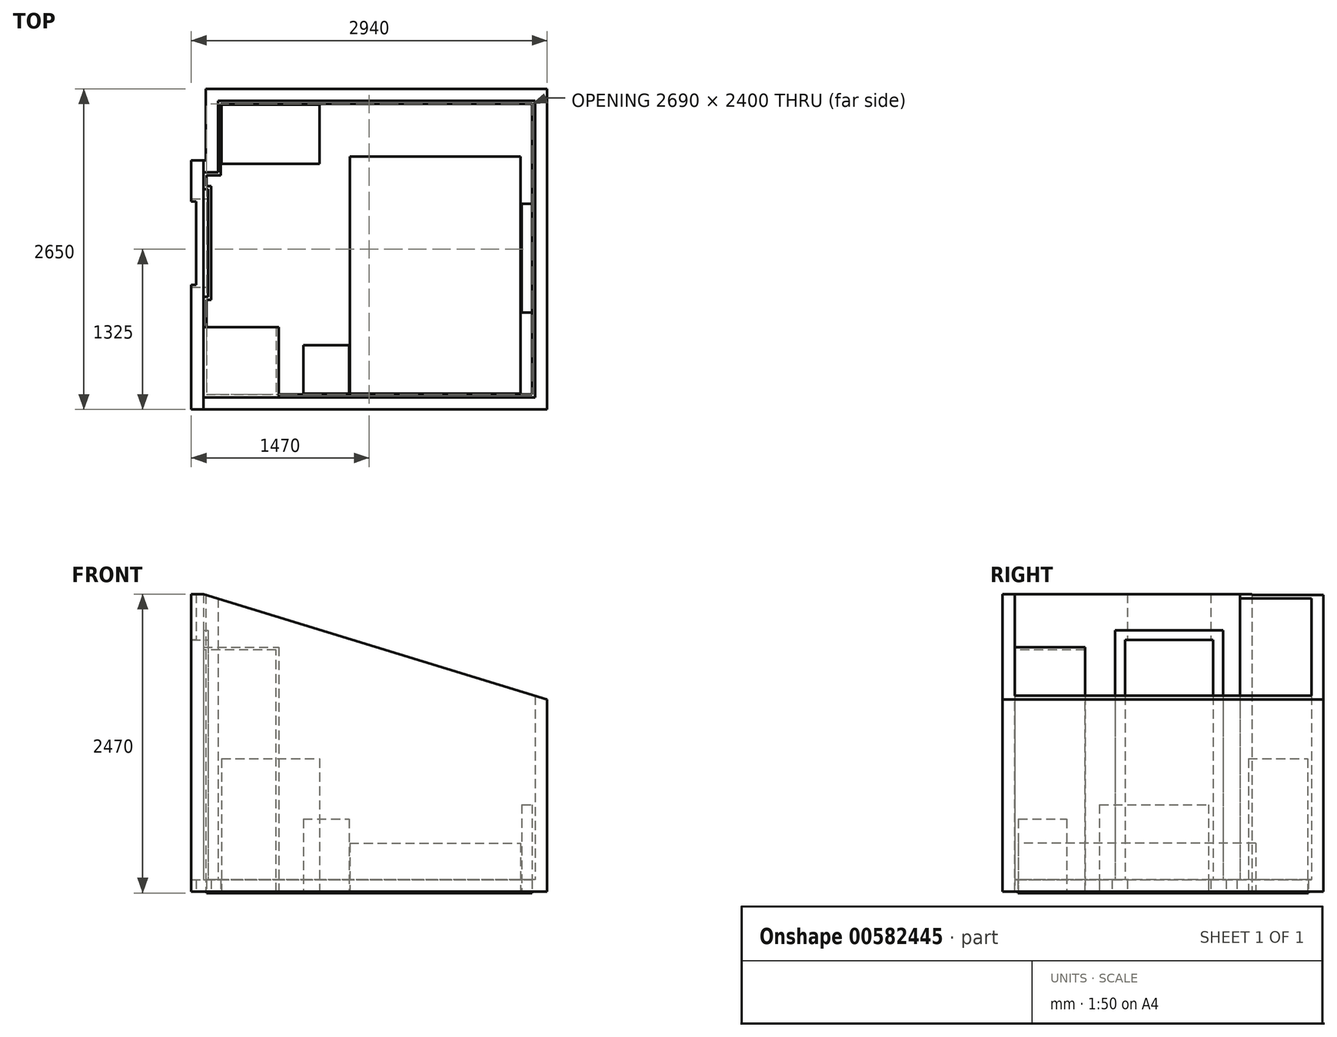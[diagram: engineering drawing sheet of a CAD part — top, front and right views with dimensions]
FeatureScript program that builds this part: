
annotation { "Feature Type Name" : "Feature", "Feature Type Description" : "" }
export const myFeature = defineFeature(function(context is Context, id is Id, definition is map)
    precondition{}
    {
        {
            var Q0;
            Q0=qCreatedBy(makeId("Top.planeOp"),FACE);
            var sketch = newSketch(context, id + "F0", { "sketchPlane" : qUnion([Q0])});
            skLineSegment(sketch, "E0", {"start": v(-1282.9, 1384.59) * mm, "end": v(-1282.9, 794.59) * mm});
            skLineSegment(sketch, "E1", {"start": v(-1282.9, 794.59) * mm, "end": v(-1402.9, 794.59) * mm});
            skLineSegment(sketch, "E2", {"start": v(-1402.9, 794.59) * mm, "end": v(-1402.9, 654.59) * mm});
            skLineSegment(sketch, "E3", {"start": v(-1402.9, 654.59) * mm, "end": v(-1362.9, 654.59) * mm});
            skLineSegment(sketch, "E4", {"start": v(-1362.9, 654.59) * mm, "end": v(-1362.9, -235.41) * mm});
            skLineSegment(sketch, "E5", {"start": v(-1362.9, -235.41) * mm, "end": v(-1402.9, -235.41) * mm});
            skLineSegment(sketch, "E6", {"start": v(-1402.9, -235.41) * mm, "end": v(-1402.9, -1065.41) * mm});
            skLineSegment(sketch, "E7", {"start": v(-1402.9, -1065.41) * mm, "end": v(1337.1, -1065.41) * mm});
            skLineSegment(sketch, "E8", {"start": v(1337.1, -1065.41) * mm, "end": v(1337.1, 1384.59) * mm});
            skLineSegment(sketch, "E9", {"start": v(1337.1, 1384.59) * mm, "end": v(-1282.9, 1384.59) * mm});
            skLineSegment(sketch, "E10.0", {"start": v(-1502.9, -1165.41) * mm, "end": v(1437.1, -1165.41) * mm});
            skLineSegment(sketch, "E10.1", {"start": v(-1502.9, -135.41) * mm, "end": v(-1502.9, -1165.41) * mm});
            skLineSegment(sketch, "E10.2", {"start": v(1437.1, -1165.41) * mm, "end": v(1437.1, 1484.59) * mm});
            skLineSegment(sketch, "E10.3", {"start": v(-1462.9, -135.41) * mm, "end": v(-1502.9, -135.41) * mm});
            skLineSegment(sketch, "E10.4", {"start": v(-1462.9, 554.59) * mm, "end": v(-1462.9, -135.41) * mm});
            skLineSegment(sketch, "E10.5", {"start": v(-1502.9, 554.59) * mm, "end": v(-1462.9, 554.59) * mm});
            skLineSegment(sketch, "E10.6", {"start": v(1437.1, 1484.59) * mm, "end": v(-1382.9, 1484.59) * mm});
            skLineSegment(sketch, "E10.7", {"start": v(-1382.9, 1484.59) * mm, "end": v(-1382.9, 894.59) * mm});
            skLineSegment(sketch, "E10.8", {"start": v(-1382.9, 894.59) * mm, "end": v(-1502.9, 894.59) * mm});
            skLineSegment(sketch, "E10.9", {"start": v(-1502.9, 894.59) * mm, "end": v(-1502.9, 554.59) * mm});
            skLineSegment(sketch, "E11.0", {"start": v(-1257.9, 769.59) * mm, "end": v(-1377.9, 769.59) * mm});
            skLineSegment(sketch, "E11.1", {"start": v(-1257.9, 1359.59) * mm, "end": v(-1257.9, 769.59) * mm});
            skLineSegment(sketch, "E11.2", {"start": v(-1377.9, 769.59) * mm, "end": v(-1377.9, 679.59) * mm});
            skLineSegment(sketch, "E11.3", {"start": v(1312.1, 1359.59) * mm, "end": v(-1257.9, 1359.59) * mm});
            skLineSegment(sketch, "E11.4", {"start": v(1312.1, -1040.41) * mm, "end": v(1312.1, 1359.59) * mm});
            skLineSegment(sketch, "E11.5", {"start": v(-1377.9, -1040.41) * mm, "end": v(1312.1, -1040.41) * mm});
            skLineSegment(sketch, "E11.6", {"start": v(-1377.9, 679.59) * mm, "end": v(-1337.9, 679.59) * mm});
            skLineSegment(sketch, "E11.7", {"start": v(-1337.9, 679.59) * mm, "end": v(-1337.9, -260.41) * mm});
            skLineSegment(sketch, "E11.8", {"start": v(-1337.9, -260.41) * mm, "end": v(-1377.9, -260.41) * mm});
            skLineSegment(sketch, "E11.9", {"start": v(-1377.9, -260.41) * mm, "end": v(-1377.9, -1040.41) * mm});
            skLineSegment(sketch, "E12.bottom", {"start": v(1227.1, -365.41) * mm, "end": v(1312.1, -365.41) * mm});
            skLineSegment(sketch, "E12.top", {"start": v(1227.1, 534.59) * mm, "end": v(1312.1, 534.59) * mm});
            skLineSegment(sketch, "E12.left", {"start": v(1227.1, -365.41) * mm, "end": v(1227.1, 534.59) * mm});
            skLineSegment(sketch, "E12.right", {"start": v(1312.1, -365.41) * mm, "end": v(1312.1, 534.59) * mm});
            skSolve(sketch);
        }
        {
            var Q0;
            Q0=makeQuery(id+"F0.imprint","IMPRINT",FACE,{"disambiguationData":[TD([[makeQuery(id+"F0.imprint","IMPRINT",EDGE,{"derivedFrom":sQuery(id+"F0.wireOp",EDGE,"E0")}),1.0]])]});
            extrude(context, id + "F1", {"entities" : qUnion([Q0]), "depth" : 100 * mm, "offsetDistance" : 25 * mm});
        }
        {
            var Q0;
            Q0=makeQuery(id+"F0.imprint","IMPRINT",FACE,{"disambiguationData":[TD([[makeQuery(id+"F0.imprint","IMPRINT",EDGE,{"derivedFrom":sQuery(id+"F0.wireOp",EDGE,"E0")}),-1.0]])]});
            extrude(context, id + "F2", {"entities" : qUnion([Q0]), "operationType" : NewBodyOperationType.ADD, "depth" : 2460 * mm, "offsetDistance" : 25 * mm});
        }
        {
            var Q0;
            Q0=makeQuery(id+"F0.imprint","IMPRINT",FACE,{"disambiguationData":[TD([[makeQuery(id+"F0.imprint","IMPRINT",EDGE,{"derivedFrom":sQuery(id+"F0.wireOp",EDGE,"E12.bottom")}),1.0]])]});
            extrude(context, id + "F3", {"entities" : qUnion([Q0]), "operationType" : NewBodyOperationType.ADD, "depth" : 720 * mm, "offsetDistance" : 25 * mm});
        }
        {
            var Q0;
            Q0=makeQuery(id+"F0.imprint","IMPRINT",FACE,{"disambiguationData":[TD([[makeQuery(id+"F0.imprint","IMPRINT",EDGE,{"derivedFrom":sQuery(id+"F0.wireOp",EDGE,"E11.0")}),1.0]])]});
            extrude(context, id + "F4", {"entities" : qUnion([Q0]), "oppositeDirection" : true, "depth" : 10 * mm, "offsetDistance" : 25 * mm});
        }
        {
            var Q0;
            Q0=qCreatedBy(makeId("Front.planeOp"),FACE);
            var sketch = newSketch(context, id + "F5", { "sketchPlane" : qUnion([Q0])});
            skLineSegment(sketch, "E13", {"start": v(-1402.9, 2460) * mm, "end": v(1437.1, 2460) * mm});
            skLineSegment(sketch, "E14", {"start": v(1437.1, 2460) * mm, "end": v(1437.1, 1590) * mm});
            skLineSegment(sketch, "E15", {"start": v(1437.1, 1590) * mm, "end": v(-1402.9, 2460) * mm});
            skSolve(sketch);
        }
        {
            var Q0;
            Q0 = qSketchRegion(id + "F5", true);
            extrude(context, id + "F6", {"entities" : qUnion([Q0]), "operationType" : NewBodyOperationType.REMOVE, "endBound" : BoundingType.THROUGH_ALL, "oppositeDirection" : true, "depth" : 25 * mm, "offsetDistance" : 25 * mm, "hasSecondDirection" : true, "secondDirectionBound" : SecondDirectionBoundingType.THROUGH_ALL, "secondDirectionOppositeDirection" : false, "secondDirectionDepth" : 25 * mm});
        }
        {
            var Q0;
            Q0=makeQuery(id+"F2.opExtrude","SWEPT_FACE",FACE,{"disambiguationData":[OSD([sQuery(id+"F0.wireOp",EDGE,"E4")])]});
            var sketch = newSketch(context, id + "F7", { "sketchPlane" : qUnion([Q0])});
            skLineSegment(sketch, "E16.bottom", {"start": v(-235.41, 2160) * mm, "end": v(654.59, 2160) * mm});
            skLineSegment(sketch, "E16.top", {"start": v(-235.41, 2460) * mm, "end": v(654.59, 2460) * mm});
            skLineSegment(sketch, "E16.left", {"start": v(-235.41, 2160) * mm, "end": v(-235.41, 2460) * mm});
            skLineSegment(sketch, "E16.right", {"start": v(654.59, 2160) * mm, "end": v(654.59, 2460) * mm});
            skSolve(sketch);
        }
        {
            var Q0;
            Q0 = qSketchRegion(id + "F7", true);
            var Q1;
            Q1=makeQuery(id+"F2.opExtrude","SWEPT_FACE",FACE,{"disambiguationData":[OSD([sQuery(id+"F0.wireOp",EDGE,"E6")])]});
            extrude(context, id + "F8", {"entities" : qUnion([Q0]), "operationType" : NewBodyOperationType.REMOVE, "endBound" : BoundingType.UP_TO_SURFACE, "oppositeDirection" : true, "depth" : 25 * mm, "endBoundEntityFace" : qUnion([Q1]), "offsetDistance" : 25 * mm});
        }
        {
            var Q0;
            Q0=makeQuery(id+"F2.opExtrude","SWEPT_FACE",FACE,{"disambiguationData":[OSD([sQuery(id+"F0.wireOp",EDGE,"E4")])]});
            var sketch = newSketch(context, id + "F9", { "sketchPlane" : qUnion([Q0])});
            skLineSegment(sketch, "E17.bottom", {"start": v(-155.41, 2080) * mm, "end": v(574.59, 2080) * mm});
            skLineSegment(sketch, "E17.top", {"start": v(-155.41, 100) * mm, "end": v(574.59, 100) * mm});
            skLineSegment(sketch, "E17.left", {"start": v(-155.41, 2080) * mm, "end": v(-155.41, 100) * mm});
            skLineSegment(sketch, "E17.right", {"start": v(574.59, 2080) * mm, "end": v(574.59, 100) * mm});
            skSolve(sketch);
        }
        {
            var Q0;
            Q0=makeQuery(id+"F9.imprint","IMPRINT",FACE,{"disambiguationData":[TD([[makeQuery(id+"F9.imprint","IMPRINT",EDGE,{"derivedFrom":sQuery(id+"F9.wireOp",EDGE,"E17.bottom")}),-1.0]])]});
            extrude(context, id + "F10", {"entities" : qUnion([Q0]), "operationType" : NewBodyOperationType.REMOVE, "endBound" : BoundingType.THROUGH_ALL, "oppositeDirection" : true, "depth" : 25 * mm, "offsetDistance" : 25 * mm});
        }
        {
            var Q0;
            Q0=makeQuery(id+"F2.opExtrude","CAP_FACE",FACE,{"disambiguationData":[OSD([sQuery(id+"F0.wireOp",EDGE,"E0"),sQuery(id+"F0.wireOp",EDGE,"E1"),sQuery(id+"F0.wireOp",EDGE,"E2"),sQuery(id+"F0.wireOp",EDGE,"E3"),sQuery(id+"F0.wireOp",EDGE,"E4"),sQuery(id+"F0.wireOp",EDGE,"E5"),sQuery(id+"F0.wireOp",EDGE,"E6"),sQuery(id+"F0.wireOp",EDGE,"E7"),sQuery(id+"F0.wireOp",EDGE,"E8"),sQuery(id+"F0.wireOp",EDGE,"E9"),sQuery(id+"F0.wireOp",EDGE,"E10.0"),sQuery(id+"F0.wireOp",EDGE,"E10.1"),sQuery(id+"F0.wireOp",EDGE,"E10.2"),sQuery(id+"F0.wireOp",EDGE,"E10.3"),sQuery(id+"F0.wireOp",EDGE,"E10.4"),sQuery(id+"F0.wireOp",EDGE,"E10.5"),sQuery(id+"F0.wireOp",EDGE,"E10.6"),sQuery(id+"F0.wireOp",EDGE,"E10.7"),sQuery(id+"F0.wireOp",EDGE,"E10.8"),sQuery(id+"F0.wireOp",EDGE,"E10.9")])],"isStart":false});
            var sketch = newSketch(context, id + "F11", { "sketchPlane" : qUnion([Q0])});
            skLineSegment(sketch, "E18.bottom", {"start": v(-1669.37, 137.35) * mm, "end": v(1973.1, 137.35) * mm});
            skLineSegment(sketch, "E18.top", {"start": v(-1669.37, -1712.3) * mm, "end": v(1973.1, -1712.3) * mm});
            skLineSegment(sketch, "E18.left", {"start": v(-1669.37, 137.35) * mm, "end": v(-1669.37, -1712.3) * mm});
            skLineSegment(sketch, "E18.right", {"start": v(1973.1, 137.35) * mm, "end": v(1973.1, -1712.3) * mm});
            skLineSegment(sketch, "E19.bottom", {"start": v(1973.1, 137.35) * mm, "end": v(-1669.37, 137.35) * mm});
            skLineSegment(sketch, "E19.top", {"start": v(1973.1, 1732.25) * mm, "end": v(-1669.37, 1732.25) * mm});
            skLineSegment(sketch, "E19.left", {"start": v(1973.1, 137.35) * mm, "end": v(1973.1, 1732.25) * mm});
            skLineSegment(sketch, "E19.right", {"start": v(-1669.37, 137.35) * mm, "end": v(-1669.37, 1732.25) * mm});
            skSolve(sketch);
        }
        {
            var Q0;
            Q0=makeQuery(id+"F0.imprint","IMPRINT",FACE,{"disambiguationData":[TD([[makeQuery(id+"F0.imprint","IMPRINT",EDGE,{"derivedFrom":sQuery(id+"F0.wireOp",EDGE,"E11.0")}),1.0]])]});
            var sketch = newSketch(context, id + "F12", { "sketchPlane" : qUnion([Q0])});
            skLineSegment(sketch, "E20.bottom", {"start": v(-192.9, 924.59) * mm, "end": v(1217.1, 924.59) * mm});
            skLineSegment(sketch, "E20.top", {"start": v(-192.9, -1035.41) * mm, "end": v(1217.1, -1035.41) * mm});
            skLineSegment(sketch, "E20.left", {"start": v(-192.9, 924.59) * mm, "end": v(-192.9, -1035.41) * mm});
            skLineSegment(sketch, "E20.right", {"start": v(1217.1, 924.59) * mm, "end": v(1217.1, -1035.41) * mm});
            skLineSegment(sketch, "E21.bottom", {"start": v(-1252.9, 864.59) * mm, "end": v(-442.9, 864.59) * mm});
            skLineSegment(sketch, "E21.top", {"start": v(-1252.9, 1354.59) * mm, "end": v(-442.9, 1354.59) * mm});
            skLineSegment(sketch, "E21.left", {"start": v(-1252.9, 864.59) * mm, "end": v(-1252.9, 1354.59) * mm});
            skLineSegment(sketch, "E21.right", {"start": v(-442.9, 864.59) * mm, "end": v(-442.9, 1354.59) * mm});
            skLineSegment(sketch, "E22.bottom", {"start": v(-577.9, -1035.41) * mm, "end": v(-197.9, -1035.41) * mm});
            skLineSegment(sketch, "E22.top", {"start": v(-577.9, -635.41) * mm, "end": v(-197.9, -635.41) * mm});
            skLineSegment(sketch, "E22.left", {"start": v(-577.9, -1035.41) * mm, "end": v(-577.9, -635.41) * mm});
            skLineSegment(sketch, "E22.right", {"start": v(-197.9, -1035.41) * mm, "end": v(-197.9, -635.41) * mm});
            skSolve(sketch);
        }
        {
            var Q0;
            Q0=makeQuery(id+"F12.imprint","IMPRINT",FACE,{"disambiguationData":[TD([[makeQuery(id+"F12.imprint","IMPRINT",EDGE,{"derivedFrom":sQuery(id+"F12.wireOp",EDGE,"E21.bottom")}),1.0]])]});
            extrude(context, id + "F13", {"entities" : qUnion([Q0]), "depth" : 1100 * mm, "offsetDistance" : 25 * mm});
        }
        {
            var Q0;
            Q0=makeQuery(id+"F12.imprint","IMPRINT",FACE,{"disambiguationData":[TD([[makeQuery(id+"F12.imprint","IMPRINT",EDGE,{"derivedFrom":sQuery(id+"F12.wireOp",EDGE,"E20.bottom")}),-1.0]])]});
            extrude(context, id + "F14", {"entities" : qUnion([Q0]), "depth" : 400 * mm, "offsetDistance" : 25 * mm});
        }
        {
            var Q0;
            Q0=makeQuery(id+"F12.imprint","IMPRINT",FACE,{"disambiguationData":[TD([[makeQuery(id+"F12.imprint","IMPRINT",EDGE,{"derivedFrom":sQuery(id+"F12.wireOp",EDGE,"E22.bottom")}),1.0]])]});
            extrude(context, id + "F15", {"entities" : qUnion([Q0]), "depth" : 600 * mm, "offsetDistance" : 25 * mm});
        }
        {
            var Q0;
            Q0=makeQuery(id+"F2.opExtrude","SWEPT_FACE",FACE,{"disambiguationData":[OSD([sQuery(id+"F0.wireOp",EDGE,"E7")])]});
            var sketch = newSketch(context, id + "F16", { "sketchPlane" : qUnion([Q0])});
            skLineSegment(sketch, "E23", {"start": v(1402.9, 2000) * mm, "end": v(1402.9, 2022) * mm});
            skLineSegment(sketch, "E24", {"start": v(1402.9, 2022) * mm, "end": v(780.9, 2022) * mm});
            skLineSegment(sketch, "E25", {"start": v(780.9, 2022) * mm, "end": v(780.9, 0) * mm});
            skLineSegment(sketch, "E26", {"start": v(780.9, 0) * mm, "end": v(802.9, 0) * mm});
            skLineSegment(sketch, "E27", {"start": v(802.9, 0) * mm, "end": v(802.9, 2000) * mm});
            skLineSegment(sketch, "E28", {"start": v(802.9, 2000) * mm, "end": v(1402.9, 2000) * mm});
            skSolve(sketch);
        }
        {
            var Q0;
            Q0 = qSketchRegion(id + "F16", true);
            extrude(context, id + "F17", {"entities" : qUnion([Q0]), "depth" : 580 * mm, "offsetDistance" : 25 * mm});
        }
    });
